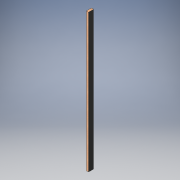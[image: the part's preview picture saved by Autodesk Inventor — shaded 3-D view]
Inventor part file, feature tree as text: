
AUTODESK INVENTOR PART (.ipt)
format: ipt  version: 2017 (Build 210142000, 142)  size: 120,832 bytes
history: native  units: in
note: dims shown in document units (in); Inventor stores cm internally (conversion verified against a paired STEP export)
features: extrude x3, sketch x3
ambient origin geometry x8: Origin, YZ Plane, XZ Plane, XY Plane, X Axis, Y Axis, Z Axis, Center Point
bodies: Solid1 (feature_tree)
feature tree (6):
  extrude  "Extrusion1"  Depth=3.5in
  extrude  "Extrusion4"  Depth=94.5in
  extrude  "Extrusion5"  Depth=1.5in
  sketch  "Sketch1"  dims[d0=1.5in d1=3.5in]
  sketch  "Sketch4"  dims[d2=94.5in d3=0.0in d12=0.1875in]
  sketch  "Sketch5"  dims[d13=1.5in d14=0.0in d15=1.5in d16=0.1875in d17=1.5in d18=0.0in]
